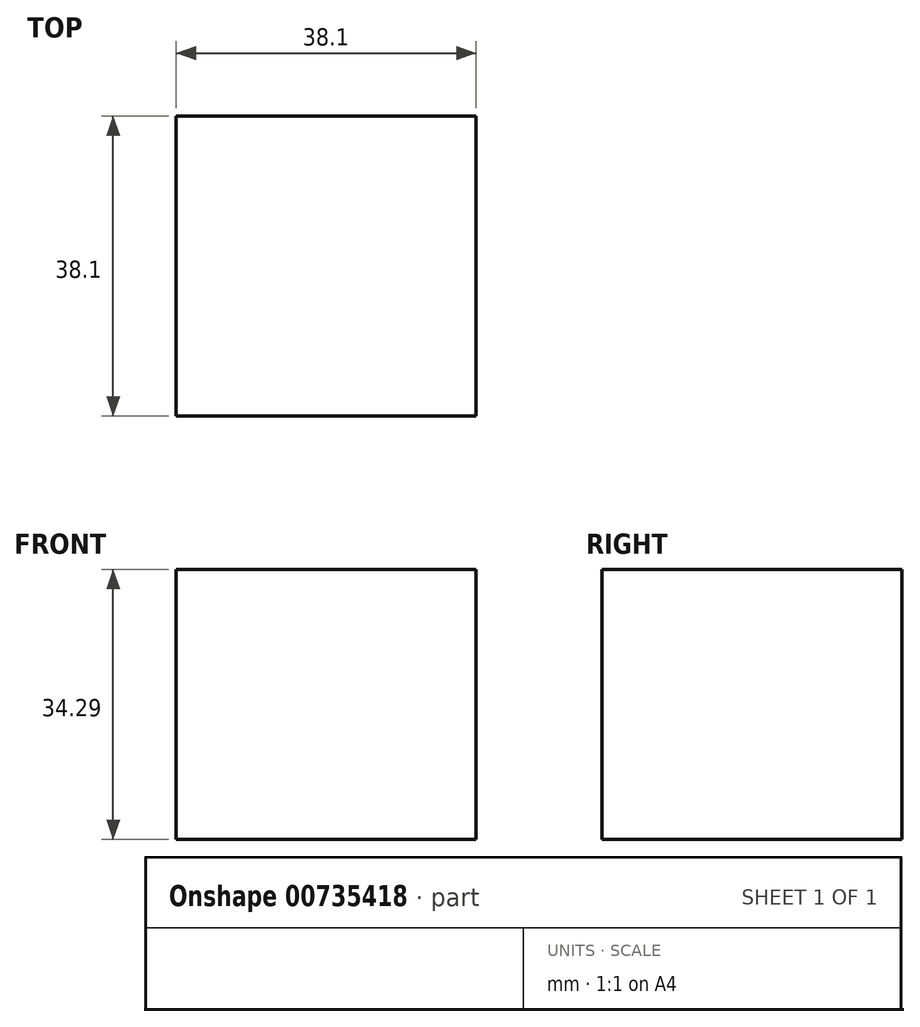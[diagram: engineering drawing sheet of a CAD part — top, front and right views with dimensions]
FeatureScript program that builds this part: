
annotation { "Feature Type Name" : "Feature", "Feature Type Description" : "" }
export const myFeature = defineFeature(function(context is Context, id is Id, definition is map)
    precondition{}
    {
        {
            var Q0;
            Q0=qCreatedBy(makeId("Top.planeOp"),FACE);
            var sketch = newSketch(context, id + "F0", { "sketchPlane" : qUnion([Q0])});
            skCircle(sketch, "E0", {"center": v(0, 0) * mm, "radius": 56.59 * mm});
            skLineSegment(sketch, "E1.bottom", {"start": v(-19.05, 19.05) * mm, "end": v(19.05, 19.05) * mm});
            skLineSegment(sketch, "E1.top", {"start": v(-19.05, -19.05) * mm, "end": v(19.05, -19.05) * mm});
            skLineSegment(sketch, "E1.left", {"start": v(-19.05, 19.05) * mm, "end": v(-19.05, -19.05) * mm});
            skLineSegment(sketch, "E1.right", {"start": v(19.05, 19.05) * mm, "end": v(19.05, -19.05) * mm});
            skSolve(sketch);
        }
        {
            var Q0;
            Q0=makeQuery(id+"F0.imprint","IMPRINT",FACE,{"disambiguationData":[TD([[makeQuery(id+"F0.imprint","IMPRINT",EDGE,{"derivedFrom":sQuery(id+"F0.wireOp",EDGE,"E1.bottom")}),-1.0]])]});
            extrude(context, id + "F1", {"entities" : qUnion([Q0]), "depth" : 34.3 * mm, "offsetDistance" : 25.4 * mm});
        }
    });
